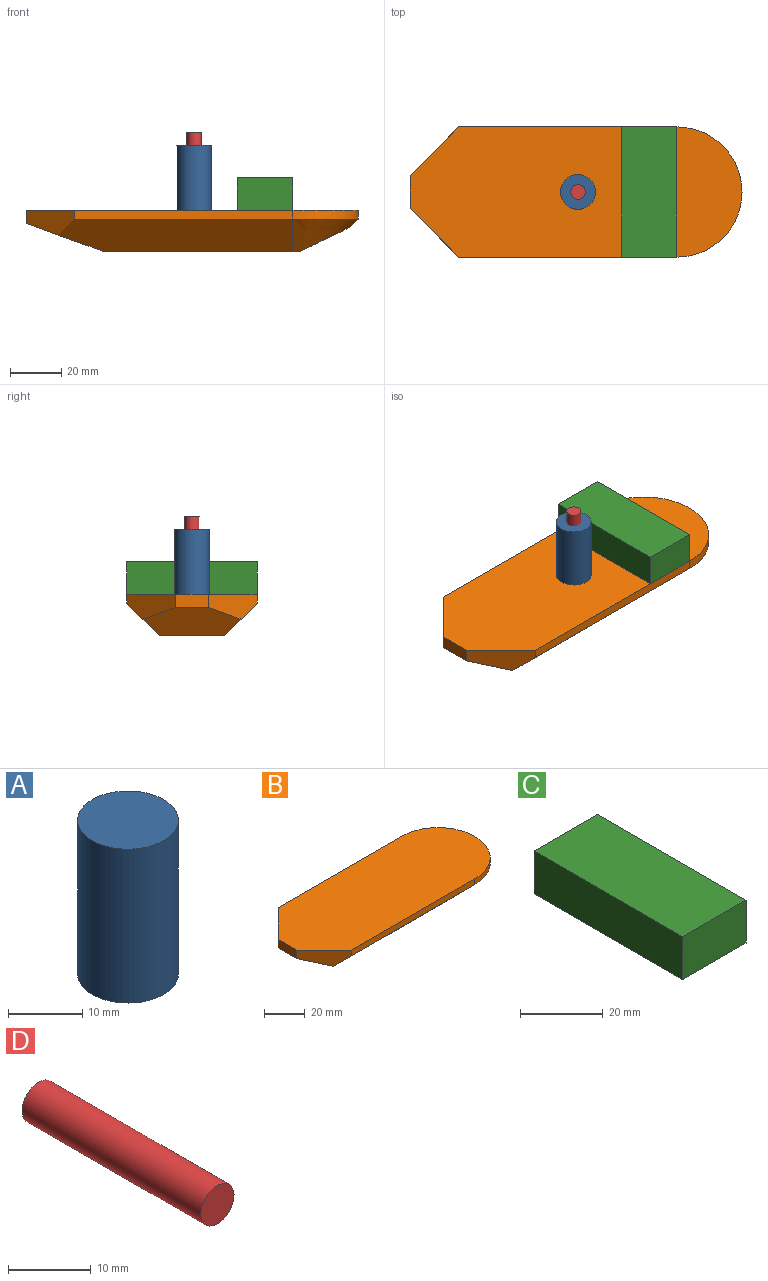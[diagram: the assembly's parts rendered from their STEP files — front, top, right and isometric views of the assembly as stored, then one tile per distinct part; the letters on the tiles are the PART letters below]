
ASSEMBLY  parts=4 mates=3
PART A: 3 faces, bbox 13.6x13.6x25.4 mm
  f0: cylinder r=6.8mm len=25.4mm, axis (0,0,-1), area 1085.5mm2, adj f1,f2
  f1: plane 13.6x13.6mm, normal (0,0,1), area 145.4mm2, adj f0
  f2: plane 13.6x13.6mm, normal (0,0,-1), area 145.4mm2, adj f0
PART B: 13 faces, bbox 129.5x50.8x16.2 mm
  f0: plane 12.7x5.08mm, normal (-1,0,0), area 64.5mm2, adj f1,f4,f8,f9
  f1: plane 38.26x30.48mm, normal (-0.34,0,-0.94), area 945.8mm2, adj f0,f2,f8,f9,f10,f11
  f2: plane 76.2x25.4mm, normal (0,0,-1), area 1935mm2, adj f1,f3,f10,f11,f12
  f3: plane 26.22x19.7mm, normal (0.44,0,-0.9), area 478mm2, adj f2,f12
  f4: plane 129.54x50.8mm, normal (0,0,1), area 5940.8mm2, adj f0,f5,f6,f7,f8,f9
  f5: plane 85.09x3.45mm, normal (0,-1,0), area 293.7mm2, adj f4,f7,f9,f10
  f6: plane 85.09x3.45mm, normal (0,1,0), area 293.7mm2, adj f4,f7,f8,f11
  f7: cylinder r=25.4mm len=50.8mm, axis (0,0,-1), area 275.4mm2, adj f4,f5,f6,f12
  f8: plane 19.05x19.05mm, normal (-0.71,0.71,0), area 192.2mm2, adj f0,f1,f4,f6,f11
  f9: plane 19.05x19.05mm, normal (-0.71,-0.71,0), area 192.2mm2, adj f0,f1,f4,f5,f10
  f10: plane 91.36x12.7mm, normal (0,-0.71,-0.71), area 1532.6mm2, adj f1,f2,f5,f9,f12
  f11: plane 91.36x12.7mm, normal (0,0.71,-0.71), area 1532.6mm2, adj f1,f2,f6,f8,f12
  f12: cone r=12.7mm half-angle=45deg, axis (0,0,1), area 734.2mm2, adj f2,f3,f7,f10,f11
PART C: 6 faces, bbox 21.7x50.8x12.7 mm
  f0: plane 50.8x21.69mm, normal (0,0,1), area 1101.7mm2, adj f1,f3,f4,f5
  f1: plane 50.8x12.7mm, normal (-1,0,0), area 645.2mm2, adj f0,f2,f4,f5
  f2: plane 50.8x21.69mm, normal (0,0,-1), area 1101.7mm2, adj f1,f3,f4,f5
  f3: plane 50.8x12.7mm, normal (1,0,0), area 645.2mm2, adj f0,f2,f4,f5
  f4: plane 21.69x12.7mm, normal (0,-1,0), area 275.4mm2, adj f0,f1,f2,f3
  f5: plane 21.69x12.7mm, normal (0,1,0), area 275.4mm2, adj f0,f1,f2,f3
PART D: 3 faces, bbox 5.7x30.5x5.7 mm
  f0: cylinder r=2.83mm len=30.48mm, axis (0,1,0), area 541.1mm2, adj f1,f2
  f1: plane 5.65x5.65mm, normal (0,-1,0), area 25.1mm2, adj f0
  f2: plane 5.65x5.65mm, normal (0,1,0), area 25.1mm2, adj f0
PLACE A t=(163.36,95.17,27.83)mm
PLACE B t=(29.97,17.19,11.67)mm
PLACE C t=(67.08,42.59,70.2)mm
PLACE D rot(axis=(1,0,0),90deg) t=(161.07,34.67,58.31)mm
MATE fastened D.f0 <-> B.f4  axis (0,0,1) through (22.39,17.19,27.83)mm
MATE fastened C.f2 <-> B.f4  axis (0,0,-1) through (60.94,-8.21,27.83)mm
MATE fastened A.f0 <-> B.f4  axis (0,0,-1) through (22.39,17.19,27.83)mm
